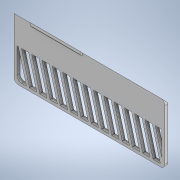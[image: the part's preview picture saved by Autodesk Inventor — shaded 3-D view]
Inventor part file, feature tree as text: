
AUTODESK INVENTOR PART (.ipt)
format: ipt  version: 2021 (Build 250183000, 183)  size: 385,024 bytes
history: native  units: mm
features: extrude x10, sketch x10, fillet x2, chamfer x1
ambient origin geometry x8: Origin, YZ Plane, XZ Plane, XY Plane, X Axis, Y Axis, Z Axis, Center Point
bodies: Solid1 (feature_tree)
feature tree (23):
  extrude  "Extrusion1"  Depth=100.0mm
  extrude  "Extrusion2"  Depth=50.0mm
  extrude  "Extrusion3"  Depth=2.0mm
  extrude  "Extrusion5"  Depth=2.0mm
  extrude  "Extrusion6"  TaperAngle=75.0deg  [1 undecoded]
  fillet  "Fillet3"  Radius=2.0mm
  extrude  "Extrusion7"  Depth=2.0mm
  fillet  "Fillet4"  Radius=2.0mm
  extrude  "Extrusion8"  Depth=2.0mm
  extrude  "Extrusion9"  Depth=2.0mm
  extrude  "Extrusion10"  Depth=2.0mm
  extrude  "Extrusion11"  Depth=2.0mm
  chamfer  "Chamfer2"  Distance=2.0mm
  sketch  "Sketch1"  dims[d0=39.5mm d1=100.0mm]
  sketch  "Sketch2"  dims[d2=19.75mm d3=50.0mm]
  sketch  "Sketch3"  dims[d4=2.0mm d5=2.0mm]
  sketch  "Sketch5"  dims[d6=2.0mm d7=2.0mm]
  sketch  "Sketch6"  dims[d8=2.0mm d9=0.0mm d11=75.0deg d12=2.0mm]
  sketch  "Sketch7"  dims[d13=2.0mm d14=2.0mm d15=2.0mm]
  sketch  "Sketch8"  dims[d16=2.0mm d17=2.0mm]
  sketch  "Sketch9"  dims[d18=2.0mm d19=2.0mm]
  sketch  "Sketch10"  dims[d20=2.0mm d21=2.0mm]
  sketch  "Sketch11"  dims[d22=2.0mm d23=2.0mm d24=2.0mm d25=2.0mm d26=2.0mm d27=2.0mm d28=0.0mm d33=2.0mm d34=4.591645mm d35=5.592mm d36=2.0mm d37=0.0mm d41=2.0mm d42=0.0mm d43=300.0mm d44=0.0mm d45=3.0mm d46=3.0mm d47=3.0mm d48=300.0mm d49=0.0mm d50=3.0mm d51=20.0mm d52=2.0mm d53=0.0mm d54=97.0mm d55=0.0mm d56=50.0mm d57=12.0mm d58=2.0mm d59=48.0mm d60=0.4mm d61=0.0mm d62=12.1mm d63=33.0mm d64=1.8mm d65=2.0mm d66=1.2mm d67=0.0mm d68=1.2mm d69=2.0mm d70=8.726646mm d39=0.5mm d40=0.872665mm]
note: 1 required parameter value undecoded (feature->parameter linkage not recoverable at this tier; creation-order binding heuristic only, values carry confidence <= 0.55)
